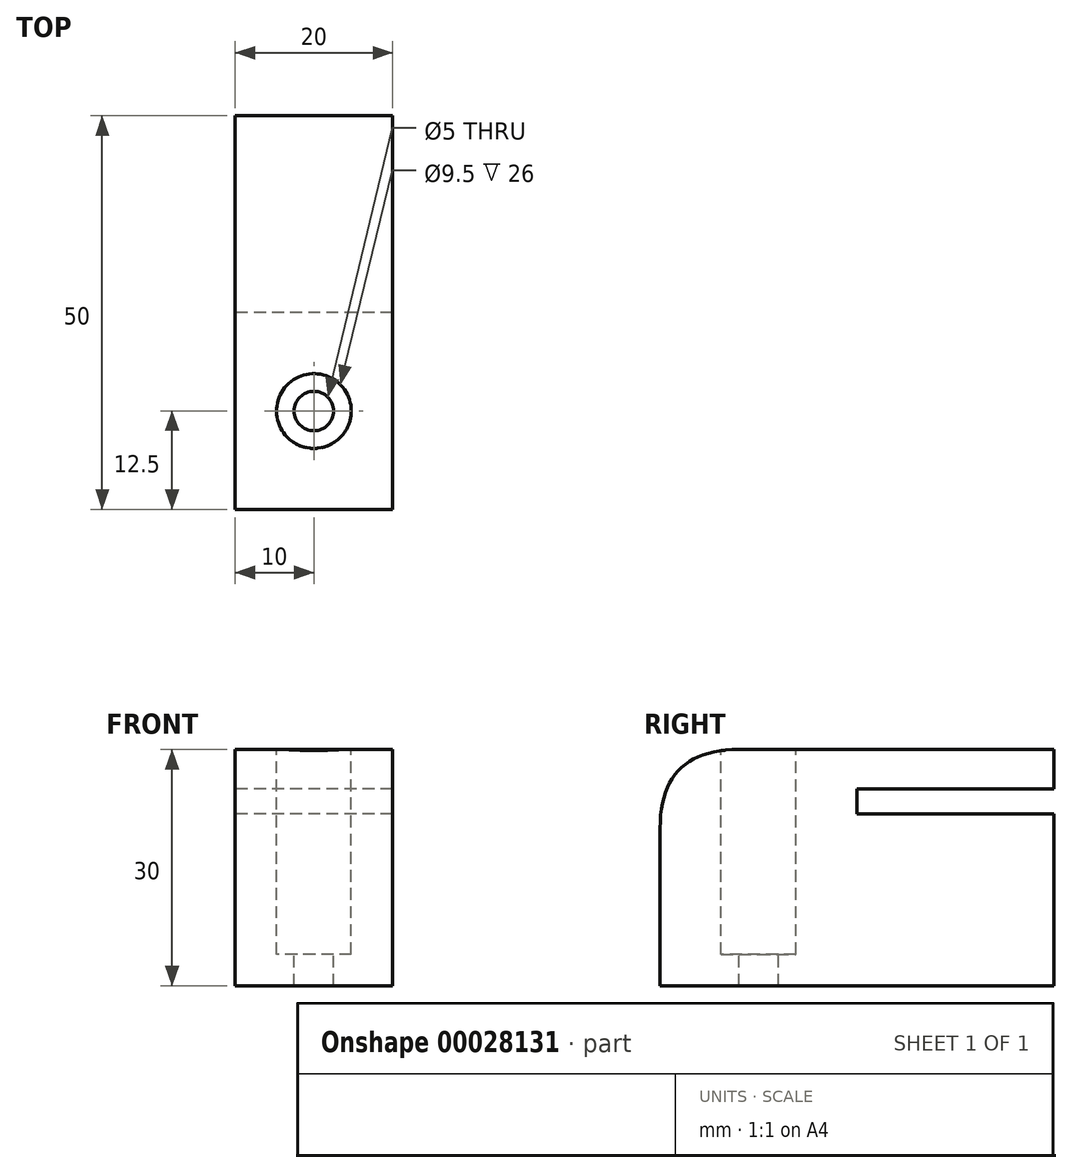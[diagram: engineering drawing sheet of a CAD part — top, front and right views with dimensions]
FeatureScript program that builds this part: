
annotation { "Feature Type Name" : "Feature", "Feature Type Description" : "" }
export const myFeature = defineFeature(function(context is Context, id is Id, definition is map)
    precondition{}
    {
        {
            var Q0;
            Q0=qCreatedBy(makeId("Top.planeOp"),FACE);
            var sketch = newSketch(context, id + "F0", { "sketchPlane" : qUnion([Q0])});
            skLineSegment(sketch, "E0.rect.bottom", {"start": v(10, -25) * mm, "end": v(-10, -25) * mm});
            skLineSegment(sketch, "E0.rect.top", {"start": v(10, 25) * mm, "end": v(-10, 25) * mm});
            skLineSegment(sketch, "E0.rect.left", {"start": v(10, -25) * mm, "end": v(10, 25) * mm});
            skLineSegment(sketch, "E0.rect.right", {"start": v(-10, -25) * mm, "end": v(-10, 25) * mm});
            skPoint(sketch, "E0.rect.middle", {"position": v(0, 0) * mm});
            skSolve(sketch);
        }
        {
            var Q0;
            Q0=makeQuery(id+"F0.imprint","IMPRINT",FACE,{"disambiguationData":[TD([[makeQuery(id+"F0.imprint","IMPRINT",EDGE,{"derivedFrom":sQuery(id+"F0.wireOp",EDGE,"E0.rect.bottom")}),-1.0]])]});
            extrude(context, id + "F1", {"entities" : qUnion([Q0]), "depth" : 20 * mm});
        }
        {
            var Q0;
            Q0=makeQuery(id+"F1.opExtrude","SWEPT_FACE",FACE,{"disambiguationData":[OSD([sQuery(id+"F0.wireOp",EDGE,"E0.rect.right")])]});
            var sketch = newSketch(context, id + "F2", { "sketchPlane" : qUnion([Q0])});
            skLineSegment(sketch, "E1.bottom", {"start": v(-25, 11.8) * mm, "end": v(0, 11.8) * mm});
            skLineSegment(sketch, "E1.top", {"start": v(-25, 15) * mm, "end": v(0, 15) * mm});
            skLineSegment(sketch, "E1.left", {"start": v(-25, 11.8) * mm, "end": v(-25, 15) * mm});
            skLineSegment(sketch, "E1.right", {"start": v(0, 11.8) * mm, "end": v(0, 15) * mm});
            skPoint(sketch, "E2", {"position": v(-25, 20) * mm});
            skSolve(sketch);
        }
        {
            var Q0;
            Q0=makeQuery(id+"F2.imprint","IMPRINT",FACE,{"disambiguationData":[TD([[makeQuery(id+"F2.imprint","IMPRINT",EDGE,{"derivedFrom":sQuery(id+"F2.wireOp",EDGE,"E1.bottom")}),1.0]])]});
            extrude(context, id + "F3", {"entities" : qUnion([Q0]), "operationType" : NewBodyOperationType.REMOVE, "oppositeDirection" : true, "depth" : 25 * mm});
        }
        {
            var Q0;
            Q0=makeQuery(id+"F1.opExtrude","CAP_FACE",FACE,{"disambiguationData":[OSD([sQuery(id+"F0.wireOp",EDGE,"E0.rect.bottom"),sQuery(id+"F0.wireOp",EDGE,"E0.rect.top"),sQuery(id+"F0.wireOp",EDGE,"E0.rect.left"),sQuery(id+"F0.wireOp",EDGE,"E0.rect.right")])],"isStart":false});
            var sketch = newSketch(context, id + "F4", { "sketchPlane" : qUnion([Q0])});
            skPoint(sketch, "E3", {"position": v(0, -25) * mm});
            skLineSegment(sketch, "E4", {"start": v(0, 0) * mm, "end": v(0, -25) * mm});
            skPoint(sketch, "E5", {"position": v(0, -12.5) * mm});
            skCircle(sketch, "E6", {"center": v(0, -12.5) * mm, "radius": 4.75 * mm});
            skSolve(sketch);
        }
        {
            var Q0;
            {var subQ0=sQuery(id+"F4.wireOp",EDGE,"E6");var subQ1=sQuery(id+"F4.wireOp",EDGE,"E4");var subQ3=makeQuery(id+"F4.imprint","INTERSECT",VERTEX,{"disambiguationData":[OD(0.0)],"derivedFrom":[subQ1,subQ0]});Q0=makeQuery(id+"F4.imprint","IMPRINT",FACE,{"disambiguationData":[TD([[makeQuery(id+"F4.imprint","IMPRINT",EDGE,{"disambiguationData":[TD([[subQ3,1.0]])],"derivedFrom":subQ1}),-1.0]])]});}
            var Q1;
            {var subQ0=sQuery(id+"F4.wireOp",EDGE,"E6");var subQ1=sQuery(id+"F4.wireOp",EDGE,"E4");var subQ3=makeQuery(id+"F4.imprint","INTERSECT",VERTEX,{"disambiguationData":[OD(0.0)],"derivedFrom":[subQ1,subQ0]});Q1=makeQuery(id+"F4.imprint","IMPRINT",FACE,{"disambiguationData":[TD([[makeQuery(id+"F4.imprint","IMPRINT",EDGE,{"disambiguationData":[TD([[subQ3,1.0]])],"derivedFrom":subQ1}),1.0]])]});}
            extrude(context, id + "F5", {"entities" : qUnion([Q0, Q1]), "operationType" : NewBodyOperationType.REMOVE, "oppositeDirection" : true, "depth" : 15 * mm});
        }
        {
            var Q0;
            Q0=makeQuery(id+"F5.boolean.opBoolean","COPY",FACE,{"derivedFrom":makeQuery(id+"F5.opExtrude","CAP_FACE",FACE,{"disambiguationData":[OSD([sQuery(id+"F4.wireOp",EDGE,"E6")])],"isStart":false})});
            var sketch = newSketch(context, id + "F6", { "sketchPlane" : qUnion([Q0])});
            skCircle(sketch, "E7", {"center": v(0, -12.5) * mm, "radius": 2.5 * mm});
            skSolve(sketch);
        }
        {
            var Q0;
            Q0=makeQuery(id+"F6.imprint","IMPRINT",FACE,{"disambiguationData":[TD([[makeQuery(id+"F6.imprint","IMPRINT",EDGE,{"derivedFrom":sQuery(id+"F6.wireOp",EDGE,"E7")}),1.0]])]});
            extrude(context, id + "F7", {"entities" : qUnion([Q0]), "operationType" : NewBodyOperationType.REMOVE, "oppositeDirection" : true, "depth" : 25 * mm});
        }
        {
            var Q0;
            Q0=makeQuery(id+"F1.opExtrude","CAP_FACE",FACE,{"disambiguationData":[OSD([sQuery(id+"F0.wireOp",EDGE,"E0.rect.bottom"),sQuery(id+"F0.wireOp",EDGE,"E0.rect.top"),sQuery(id+"F0.wireOp",EDGE,"E0.rect.left"),sQuery(id+"F0.wireOp",EDGE,"E0.rect.right")])],"isStart":true});
            extrude(context, id + "F8", {"entities" : qUnion([Q0]), "operationType" : NewBodyOperationType.ADD, "depth" : 10 * mm});
        }
        {
            var Q0;
            Q0=makeQuery(id+"F1.opExtrude","CAP_EDGE",EDGE,{"disambiguationData":[OSD([sQuery(id+"F0.wireOp",EDGE,"E0.rect.bottom")])],"isStart":false});
            fillet(context, id + "F9", {"entities" : qUnion([Q0]), "radius" : 10 * mm, "rho" : 0.5, "crossSection" : FilletCrossSection.CONIC, "allowEdgeOverflow" : false});
        }
        {
            var Q0;
            Q0=makeQuery(id+"F5.boolean.opBoolean","COPY",FACE,{"derivedFrom":makeQuery(id+"F5.opExtrude","CAP_FACE",FACE,{"disambiguationData":[OSD([sQuery(id+"F4.wireOp",EDGE,"E6")])],"isStart":false})});
            extrude(context, id + "F10", {"entities" : qUnion([Q0]), "operationType" : NewBodyOperationType.REMOVE, "oppositeDirection" : true, "depth" : 11 * mm});
        }
    });
